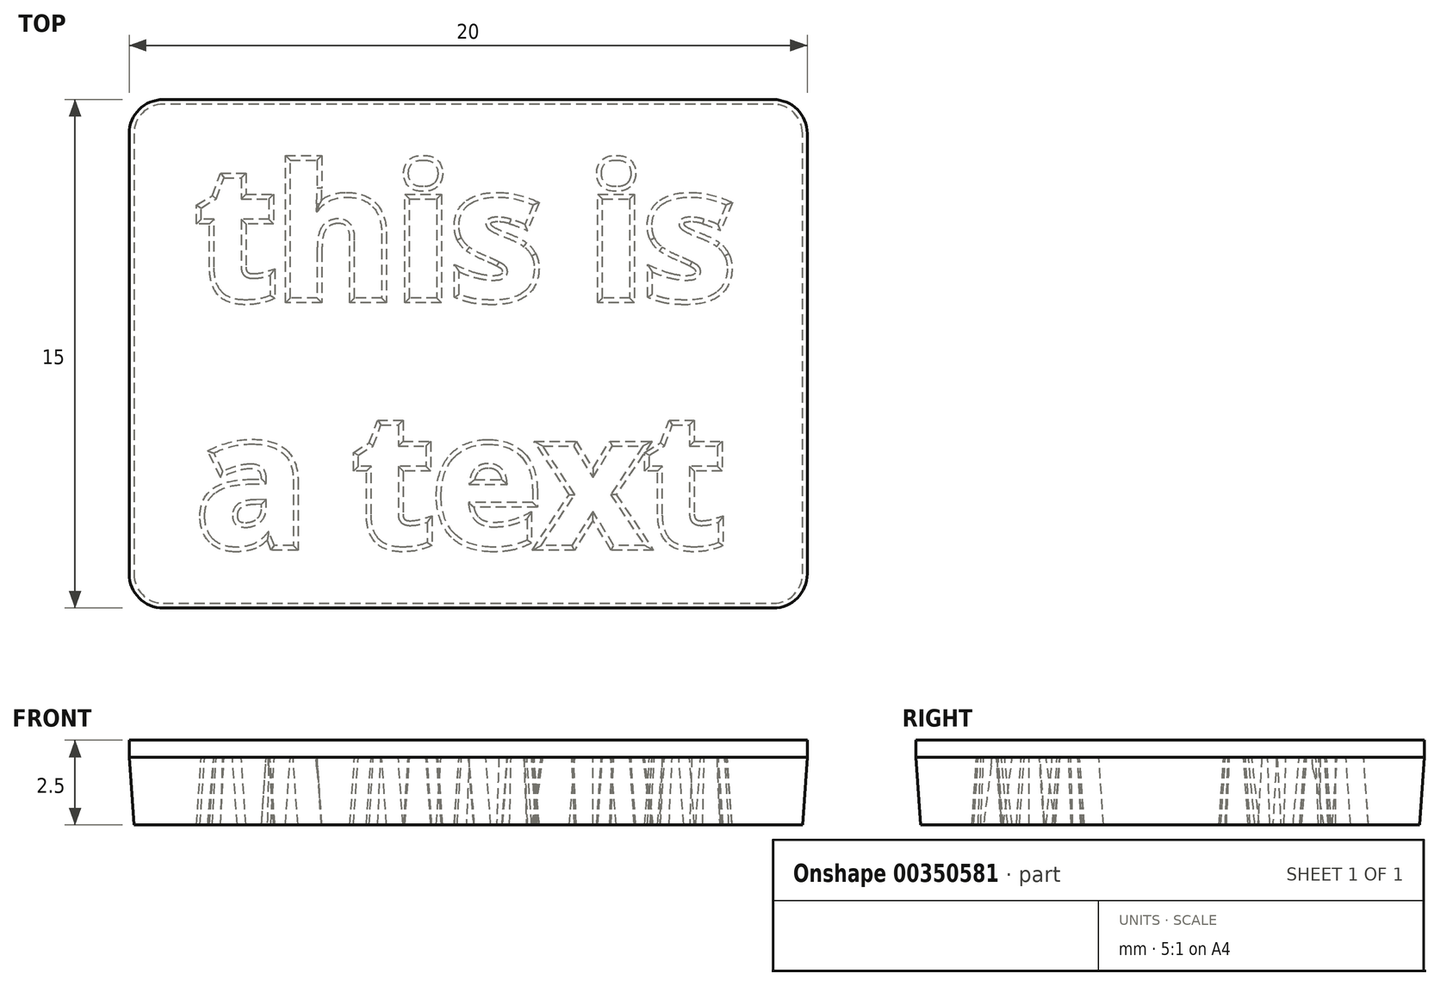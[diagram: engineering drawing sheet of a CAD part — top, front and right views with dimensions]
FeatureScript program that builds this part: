
annotation { "Feature Type Name" : "Feature", "Feature Type Description" : "" }
export const myFeature = defineFeature(function(context is Context, id is Id, definition is map)
    precondition{}
    {
        {
            var Q0;
            Q0=qCreatedBy(makeId("Top.planeOp"),FACE);
            var sketch = newSketch(context, id + "F0", { "sketchPlane" : qUnion([Q0])});
            skLineSegment(sketch, "E0.bottom", {"start": v(9, 7.5) * mm, "end": v(-9, 7.5) * mm});
            skLineSegment(sketch, "E0.top", {"start": v(9, -7.5) * mm, "end": v(-9, -7.5) * mm});
            skLineSegment(sketch, "E0.left", {"start": v(10, 6.5) * mm, "end": v(10, -6.5) * mm});
            skLineSegment(sketch, "E0.right", {"start": v(-10, 6.5) * mm, "end": v(-10, -6.5) * mm});
            skPoint(sketch, "E0.middle", {"position": v(0, 0) * mm});
            skPoint(sketch, "E1.visualSharp", {"position": v(-10, 7.5) * mm});
            skArc(sketch, "E1.filletArc", {"start": v(-9, 7.5) * mm, "mid": v(-9.7, 7.2) * mm, "end": v(-10, 6.5) * mm});
            skPoint(sketch, "E2.visualSharp", {"position": v(10, 7.5) * mm});
            skArc(sketch, "E2.filletArc", {"start": v(10, 6.5) * mm, "mid": v(9.7, 7.2) * mm, "end": v(9, 7.5) * mm});
            skPoint(sketch, "E3.visualSharp", {"position": v(10, -7.5) * mm});
            skArc(sketch, "E3.filletArc", {"start": v(9, -7.5) * mm, "mid": v(9.7, -7.2) * mm, "end": v(10, -6.5) * mm});
            skPoint(sketch, "E4.visualSharp", {"position": v(-10, -7.5) * mm});
            skArc(sketch, "E4.filletArc", {"start": v(-10, -6.5) * mm, "mid": v(-9.7, -7.2) * mm, "end": v(-9, -7.5) * mm});
            skText(sketch, "E5", { "text": "this is\na text", "fontName": "OpenSans-Bold.ttf"});
            skLineSegment(sketch, "E6", {"start": v(0, 7.5) * mm, "end": v(0, -7.5) * mm, "construction": true});
            const initialGuessF0  = {"E5": [-0.008, 0.00164, 1, 0, 0.00386]};
            skSetInitialGuess(sketch, initialGuessF0);
            skSolve(sketch);
        }
        {
            var Q0;
            Q0 = qSketchRegion(id + "F0", true);
            var Q1;
            Q1=makeQuery(id+"F0.imprint","IMPRINT",FACE,{"disambiguationData":[TD([[makeQuery(id+"F0.imprint","IMPRINT",EDGE,{"derivedFrom":sQuery(id+"F0.wireOp",EDGE,"E5.sketch_text.stroke-148")}),-1.0]])]});
            var Q2;
            Q2=makeQuery(id+"F0.imprint","IMPRINT",FACE,{"disambiguationData":[TD([[makeQuery(id+"F0.imprint","IMPRINT",EDGE,{"derivedFrom":sQuery(id+"F0.wireOp",EDGE,"E0.bottom")}),1.0]])]});
            var Q3;
            Q3=makeQuery(id+"F0.imprint","IMPRINT",FACE,{"disambiguationData":[TD([[makeQuery(id+"F0.imprint","IMPRINT",EDGE,{"derivedFrom":sQuery(id+"F0.wireOp",EDGE,"E5.sketch_text.stroke-18")}),-1.0]])]});
            var Q4;
            Q4=makeQuery(id+"F0.imprint","IMPRINT",FACE,{"disambiguationData":[TD([[makeQuery(id+"F0.imprint","IMPRINT",EDGE,{"derivedFrom":sQuery(id+"F0.wireOp",EDGE,"E5.sketch_text.stroke-40")}),-1.0]])]});
            var Q5;
            Q5=makeQuery(id+"F0.imprint","IMPRINT",FACE,{"disambiguationData":[TD([[makeQuery(id+"F0.imprint","IMPRINT",EDGE,{"derivedFrom":sQuery(id+"F0.wireOp",EDGE,"E5.sketch_text.stroke-44")}),-1.0]])]});
            var Q6;
            Q6=makeQuery(id+"F0.imprint","IMPRINT",FACE,{"disambiguationData":[TD([[makeQuery(id+"F0.imprint","IMPRINT",EDGE,{"derivedFrom":sQuery(id+"F0.wireOp",EDGE,"E5.sketch_text.stroke-75")}),-1.0]])]});
            var Q7;
            Q7=makeQuery(id+"F0.imprint","IMPRINT",FACE,{"disambiguationData":[TD([[makeQuery(id+"F0.imprint","IMPRINT",EDGE,{"derivedFrom":sQuery(id+"F0.wireOp",EDGE,"E5.sketch_text.stroke-79")}),-1.0]])]});
            var Q8;
            Q8=makeQuery(id+"F0.imprint","IMPRINT",FACE,{"disambiguationData":[TD([[makeQuery(id+"F0.imprint","IMPRINT",EDGE,{"derivedFrom":sQuery(id+"F0.wireOp",EDGE,"E5.sketch_text.stroke-123")}),1.0]])]});
            var Q9;
            Q9=makeQuery(id+"F0.imprint","IMPRINT",FACE,{"disambiguationData":[TD([[makeQuery(id+"F0.imprint","IMPRINT",EDGE,{"derivedFrom":sQuery(id+"F0.wireOp",EDGE,"E5.sketch_text.stroke-130")}),-1.0]])]});
            var Q10;
            Q10=makeQuery(id+"F0.imprint","IMPRINT",FACE,{"disambiguationData":[TD([[makeQuery(id+"F0.imprint","IMPRINT",EDGE,{"derivedFrom":sQuery(id+"F0.wireOp",EDGE,"E5.sketch_text.stroke-168")}),-1.0]])]});
            var Q11;
            Q11=makeQuery(id+"F0.imprint","IMPRINT",FACE,{"disambiguationData":[TD([[makeQuery(id+"F0.imprint","IMPRINT",EDGE,{"derivedFrom":sQuery(id+"F0.wireOp",EDGE,"E5.sketch_text.stroke-180")}),-1.0]])]});
            var Q12;
            Q12=makeQuery(id+"F0.imprint","IMPRINT",FACE,{"disambiguationData":[TD([[makeQuery(id+"F0.imprint","IMPRINT",EDGE,{"derivedFrom":sQuery(id+"F0.wireOp",EDGE,"E5.sketch_text.stroke-105")}),-1.0]])]});
            var Q13;
            Q13=makeQuery(id+"F0.imprint","IMPRINT",FACE,{"disambiguationData":[TD([[makeQuery(id+"F0.imprint","IMPRINT",EDGE,{"derivedFrom":sQuery(id+"F0.wireOp",EDGE,"E5.sketch_text.stroke-0")}),-1.0]])]});
            var Q14;
            Q14=makeQuery(id+"F0.imprint","IMPRINT",FACE,{"disambiguationData":[TD([[makeQuery(id+"F0.imprint","IMPRINT",EDGE,{"derivedFrom":sQuery(id+"F0.wireOp",EDGE,"E5.sketch_text.stroke-35")}),-1.0]])]});
            var Q15;
            Q15=makeQuery(id+"F0.imprint","IMPRINT",FACE,{"disambiguationData":[TD([[makeQuery(id+"F0.imprint","IMPRINT",EDGE,{"derivedFrom":sQuery(id+"F0.wireOp",EDGE,"E5.sketch_text.stroke-70")}),-1.0]])]});
            var Q16;
            Q16=makeQuery(id+"F0.imprint","IMPRINT",FACE,{"disambiguationData":[TD([[makeQuery(id+"F0.imprint","IMPRINT",EDGE,{"derivedFrom":sQuery(id+"F0.wireOp",EDGE,"E5.sketch_text.stroke-148")}),1.0]])]});
            extrude(context, id + "F1", {"entities" : qUnion([Q0, Q1, Q2, Q3, Q4, Q5, Q6, Q7, Q8, Q9, Q10, Q11, Q12, Q13, Q14, Q15, Q16]), "depth" : 0.5 * mm});
        }
        {
            var Q0;
            Q0=makeQuery(id+"F0.imprint","IMPRINT",FACE,{"disambiguationData":[TD([[makeQuery(id+"F0.imprint","IMPRINT",EDGE,{"derivedFrom":sQuery(id+"F0.wireOp",EDGE,"E5.sketch_text.stroke-148")}),1.0]])]});
            var Q1;
            Q1=makeQuery(id+"F0.imprint","IMPRINT",FACE,{"disambiguationData":[TD([[makeQuery(id+"F0.imprint","IMPRINT",EDGE,{"derivedFrom":sQuery(id+"F0.wireOp",EDGE,"E5.sketch_text.stroke-123")}),1.0]])]});
            var Q2;
            Q2=makeQuery(id+"F0.imprint","IMPRINT",FACE,{"disambiguationData":[TD([[makeQuery(id+"F0.imprint","IMPRINT",EDGE,{"derivedFrom":sQuery(id+"F0.wireOp",EDGE,"E0.bottom")}),1.0]])]});
            extrude(context, id + "F2", {"entities" : qUnion([Q0, Q1, Q2]), "operationType" : NewBodyOperationType.ADD, "oppositeDirection" : true, "depth" : 2 * mm, "hasDraft" : true, "draftAngle" : 4 * degree, "draftPullDirection" : true});
        }
    });
